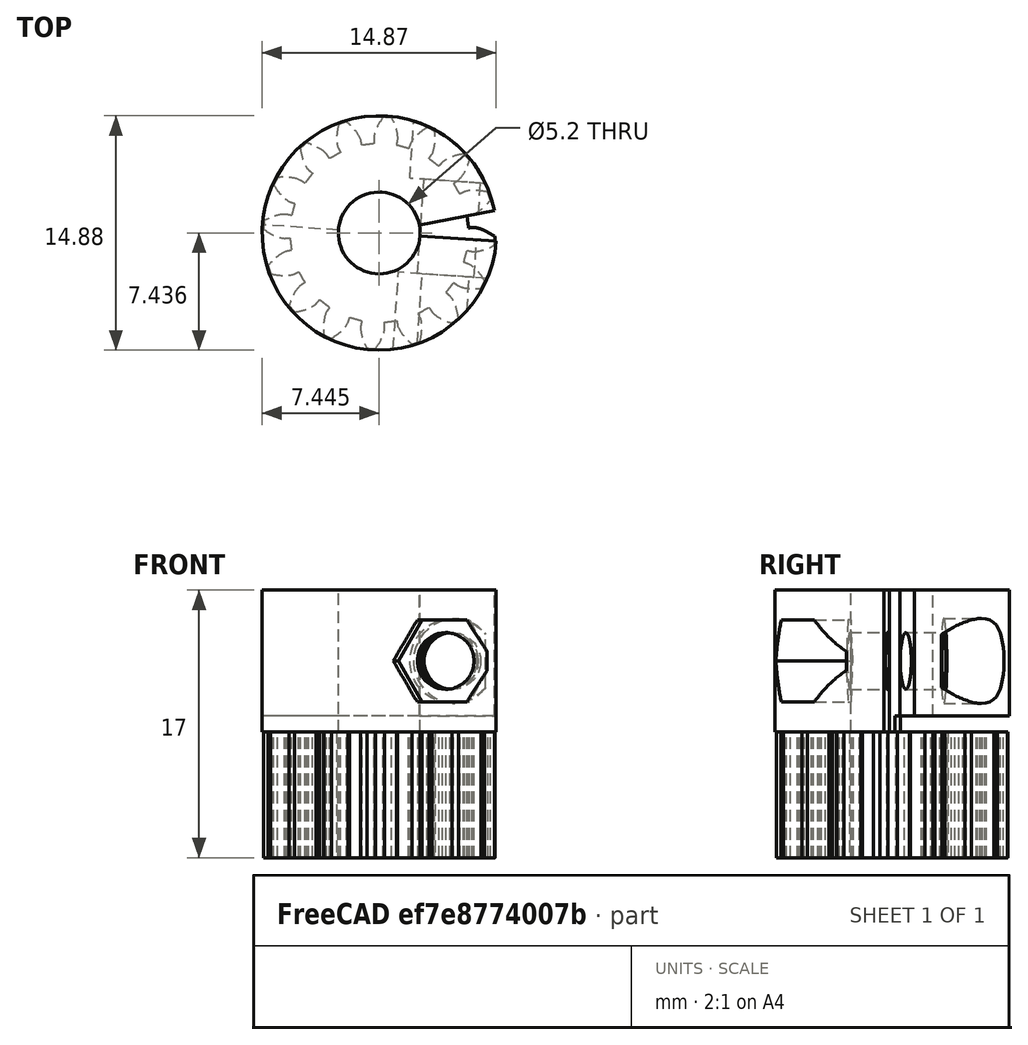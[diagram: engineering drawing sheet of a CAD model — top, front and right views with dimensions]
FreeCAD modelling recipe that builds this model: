
FCSTD DOCUMENT  (FreeCAD 0.18R16110 (Git))
Label: Pinion
License: All rights reserved
LicenseURL: http://en.wikipedia.org/wiki/All_rights_reserved
objects: Part::Cylinder×7, Part::Cut×5, Part::MultiFuse×3, Part::FeaturePython×1, Spreadsheet::Sheet×1, Part::RegularPolygon×1, Part::Extrusion×1, Mesh::Feature×1
note: 18 computed .brp shape members not serialized (recipe doc carries the construction recipe); baked Part::Feature solids carry a one-line shape summary decoded from their .brp

FEATURE [Part::FeaturePython] InvoluteGear005  # WARN: FeaturePython — macro-defined, semantics opaque (R4)
  backlash = 0
  beta = 0
  clearance = 0.2
  double_helix = false
  head = -0.1
  height = 8
  module = 0.8
  numpoints = 10
  pressure_angle = 20
  reversed_backlash = false
  shift = 0.3
  simple = false
  teeth = 16
  undercut = false
  expr: teeth = Spreadsheet.ritzel_teeth
  expr: height = Spreadsheet.z2_h
  expr: shift = Spreadsheet.ritzel_shift
  expr: module = Spreadsheet.modul
FEATURE [Part::Cylinder] Cylinder017  label="Zylinder017"
  Angle = 360
  AttacherType = Attacher::AttachEngine3D
  Height = 9
  Radius = 2.6
  expr: Radius = Spreadsheet.stepper_daxis / 2 + Spreadsheet.tolerance / 2
  expr: Height = Spreadsheet.stepper_lshaft - Spreadsheet.z2_h - 1
FEATURE [Part::Cylinder] Cylinder018  label="Zylinder018"
  Angle = 180
  AttacherType = Attacher::AttachEngine3D
  Height = 1
  Radius = 7.44
  expr: Radius = Spreadsheet.ritzel_da / 2
FEATURE [Part::Cylinder] Cylinder019  label="Zylinder019"
  Angle = 15
  AttacherType = Attacher::AttachEngine3D
  Height = 10
  Radius = 7.44
  expr: Radius = Spreadsheet.ritzel_da / 2
  expr: Height = Spreadsheet.stepper_lshaft - Spreadsheet.z2_h
FEATURE [Part::Cylinder] Cylinder016  label="Zylinder016"
  Angle = 360
  AttacherType = Attacher::AttachEngine3D
  Height = 9
  Radius = 7.44
  expr: Height = Spreadsheet.stepper_lshaft - Spreadsheet.z2_h - 1
  expr: Radius = Spreadsheet.ritzel_da / 2
FEATURE [Part::Cylinder] Cylinder020  label="Zylinder020"
  Angle = 360
  AttacherType = Attacher::AttachEngine3D
  Height = 15
  Radius = 1.8
FEATURE [Part::Cylinder] Cylinder021  label="Zylinder021"
  Angle = 360
  AttacherType = Attacher::AttachEngine3D
  Height = 6
  Placement = pos=(0,0,11) rot=(0,0,1;0rad)
  Radius = 2.7
FEATURE [Part::MultiFuse] Fusion003
  Shapes = -> [Cylinder020,Cylinder021]
FEATURE [Part::Cylinder] Cylinder002  label="Zylinder002"
  Angle = 360
  AttacherType = Attacher::AttachEngine3D
  Height = 8
  Radius = 2.6
  expr: Height = Spreadsheet.z2_h
  expr: Radius = Spreadsheet.stepper_daxis / 2 + Spreadsheet.tolerance / 2
FEATURE [Spreadsheet::Sheet] Spreadsheet
  cells = A1=Modul; B1(modul)=0.8; D1=tolerance; E1(tolerance)=0.2; G1=tolerance gear; H1(tolerance_gear)=0; A3=Zahnstange; D3=Zahnrad_1; G3=Zahnrad_2; J3=Ritzel; M3=Stepper; P3=Casing; A4=ra; B4(z_ra)=11; D4=#teeth; E4(z1_teeth)=16; G4=#teeth; H4(z2_teeth)=54; J4=#teeth; K4(ritzel_teeth)=16; M4=axis d; N4(stepper_daxis)=5; P4=gear casing sgear; Q4(casing_sgear)=2; A5=di; B5(z_ri)=8; D5=shift; E5(z1_shift)=0.2; G5=shift; H5(z2_shift)=0; J5=shift; K5(ritzel_shift)=0.3; M5=shaft l; N5(stepper_lshaft)=18; P5=rack casing srack; Q5(casing_srack)=2; A6=l; B6(z_l)==casing_ymax - casing_ymin + casing_scase; D6=pitch d; E6(z1_dpi)==modul * z1_teeth; G6=pitch d; H6(z2_dpi)==modul * z2_teeth; J6=pitch d; K6(ritzel_dpi)==modul * ritzel_teeth; M6=outside  sa; N6(stepper_sa)=28; P6=casing scase; Q6(casing_scase)=5; D7=outside d; E7(z1_da)==z1_dpi + 2 * (1 + z1_shift) * modul; G7=outside d; H7(z2_da)==z2_dpi + 2 * (1 + z2_shift) * modul; J7=outside d; K7(ritzel_da)==ritzel_dpi + 2 * (1 + ritzel_shift) * modul; M7=mount screw s; N7(stepper_sscrew)=23; P7=casing ssup; Q7(casing_ssup)=5; A8=rack height; B8(z_h)==z_th; D8=center distance; E8(z1_dc)==z1_dpi / 2 + z1_shift * modul + tolerance_gear; G8=center distance; H8(z2_dc)==z2_dpi / 2 + z2_shift * modul + tolerance_gear; J8=center distace; K8(ritzel_dc)==ritzel_dpi / 2 + ritzel_shift * modul + tolerance_gear; M8=mount d; N8(stepper_dmount)=22; P8=überlappung sjoin; Q8(casing_sjoin)=0.9; A9=rack thickness; B9(z_th)==2 * z_ra + 2; M9=mount heigth; N9(stepper_hmount)=2; A10=rack teeth width; B10(z_w)=8; D10=y Shift; E10(z1_yshift)=8; G10=height; H10(z2_h)=8; J10=angle z1; K10(ritzel_angle)=-65; M10=mount dscrew; N10(stepper_dscrew)=2.5; P10=casing y_min; Q10(casing_ymin)==-(Spreadsheet.z2_da / 2 + Spreadsheet.casing_scase + Spreadsheet.casing_sgear - Spreadsheet.z1_yshift - casing_sjoin + Spreadsheet.tolerance) * 0 + Spreadsheet.ritzel_ypos - stepper_sa / 2 - casing_scase; A11=#teeth; B11(z_teeth)=45; D11=height; E11(z1_height)==Spreadsheet.z_w * 3 / 4 + Spreadsheet.z2_dr + Spreadsheet.z2_h + Spreadsheet.z_ra; G11=distance rack; H11(z2_dr)=3; P11=casing x_min; Q11(casing_xmin)==-(Spreadsheet.z_ra * cos(asin(Spreadsheet.z_w / 2 / Spreadsheet.z_ra)) - Spreadsheet.modul + Spreadsheet.z_ra + Spreadsheet.casing_srack + Spreadsheet.casing_scase - Spreadsheet.casing_sjoin); D12=axis r; E12(z1_daxis)=2.5; G12=axis r; J12=x_pos; K12(ritzel_xpos)==Spreadsheet.z1_dc + cos(Spreadsheet.ritzel_angle) * (Spreadsheet.z2_dc + Spreadsheet.ritzel_dc); P12=casing z_min; Q12(casing_zmin)==-(Spreadsheet.z2_dr + Spreadsheet.z2_h - (Spreadsheet.z_h / 2 - Spreadsheet.z_ra) + Spreadsheet.tolerance) * 0 - 20.5; J13=y_pos; K13(ritzel_ypos)==Spreadsheet.z1_yshift + sin(Spreadsheet.ritzel_angle) * (Spreadsheet.z2_dc + Spreadsheet.ritzel_dc); G14=z_pos; H14(z2_zpos)==-(Spreadsheet.z2_dr + Spreadsheet.z2_h - (Spreadsheet.z_h / 2 - Spreadsheet.z_ra)); P14=casing z_max; Q14(casing_zmax)==(2 * Spreadsheet.casing_srack + Spreadsheet.z_th - Spreadsheet.casing_sjoin) * 0 + 44.5; G15=winkel 1; H15(z2_w1)==165°; P15=casing x_max; Q15(casing_xmax)==Spreadsheet.ritzel_xpos + stepper_sa / 2 + casing_scase + 2; A16=65; B16==-A16 / 2; C16==casing_xmax - casing_xmin - tolerance - casing_scase; G16=winkel 2; H16(z2_w2)==45°; P16=casing y_max; Q16(casing_ymax)==(Spreadsheet.ritzel_ypos + stepper_sa / 2 + 2) * 0 + 31; A17=8; B17==B16 + A18; C17==B17 ^ A20 * A19; G17=winkel 3; H17(z2_w3)==-49°; A18==A16 / A17; B18==B17 + A18; C18==B18 ^ A20 * A19; G18=winkel 4; H18(z2_w4)==-138°; A19==C16 / B16 ^ A20; B19==B18 + A18; C19==B19 ^ A20 * A19; A20=4; B20==B19 + A18; C20==B20 ^ A20 * A19; B21==B20 + A18; C21==B21 ^ A20 * A19; B22==B21 + A18; C22==B22 ^ A20 * A19; B23==B22 + A18; C23==B23 ^ A20 * A19; B24==B23 + A18; C24==B24 ^ A20 * A19
FEATURE [Part::RegularPolygon] RegularPolygon  label="Regelmäßiges Polygon"
  AttacherType = Attacher::AttachEngine3D
  Circumradius = 3
  Polygon = 6
FEATURE [Part::Extrusion] Extrude
  Base = -> RegularPolygon
  Dir = (0,0,1)
  DirMode = 2
  FaceMakerClass = Part::FaceMakerBullseye
  LengthFwd = 5
  LengthRev = 0
  Solid = true
  Symmetric = false
FEATURE [Part::MultiFuse] Fusion004
  Placement = pos=(4.4,-7.4,4.5) rot=(-1,0,0;1.5708rad)
  Shapes = -> [Fusion003,Extrude]
FEATURE [Part::Cut] Cut010
  Base = -> Cylinder016
  Tool = -> Cylinder017
FEATURE [Part::Cut] Cut001  label="Ritzel001"
  Base = -> InvoluteGear005
  Tool = -> Cylinder002
FEATURE [Part::Cut] Cut011
  Base = -> Cut010
  Tool = -> Cylinder018
FEATURE [Part::Cut] Cut012
  Base = -> Cut011
  Tool = -> Cylinder019
FEATURE [Part::Cut] Cut013
  Base = -> Cut012
  Placement = pos=(0,0,8) rot=(0,0,1;0rad)
  Tool = -> Fusion004
  expr: Placement.Base.z = Spreadsheet.z2_h
FEATURE [Part::MultiFuse] Fusion005  label="Pinion"
  Placement = pos=(18.4947,-17.5941,-10) rot=(0,0,-1;0.069813rad)
  Shapes = -> [Cut013,Cut001]
  expr: Placement.Base.z = -(Spreadsheet.z2_dr + Spreadsheet.z2_h - (Spreadsheet.z_h / 2 - Spreadsheet.z_ra))
  expr: Placement.Base.y = Spreadsheet.ritzel_ypos
  expr: Placement.Base.x = Spreadsheet.ritzel_xpos
FEATURE [Mesh::Feature] Mesh  label="Pinion (Meshed)"
